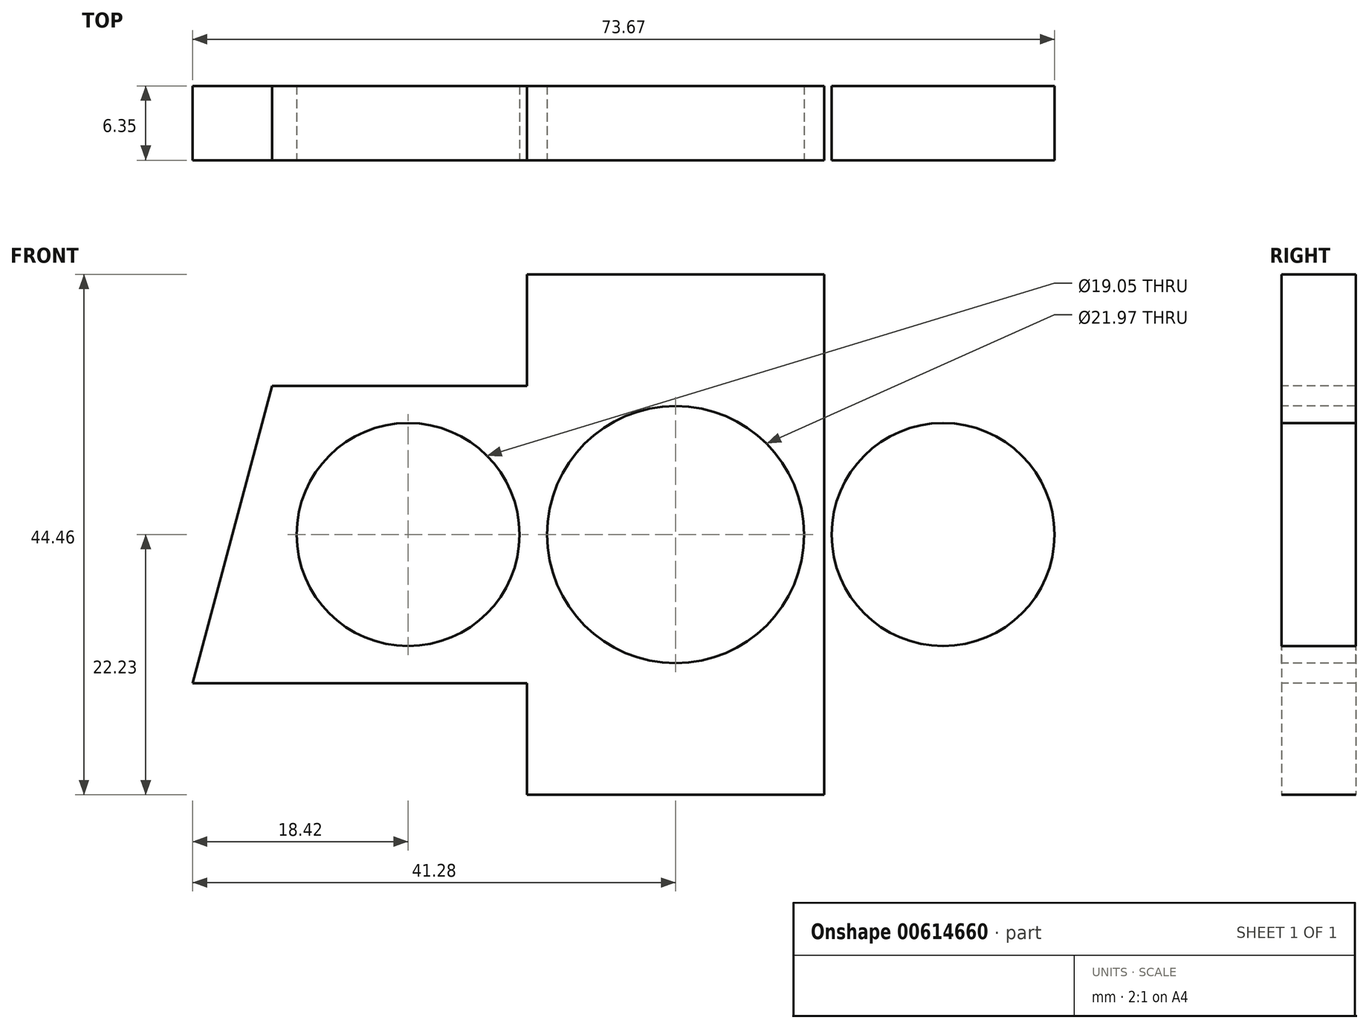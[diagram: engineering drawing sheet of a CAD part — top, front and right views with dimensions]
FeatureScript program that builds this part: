
annotation { "Feature Type Name" : "Feature", "Feature Type Description" : "" }
export const myFeature = defineFeature(function(context is Context, id is Id, definition is map)
    precondition{}
    {
        {
            var Q0;
            Q0=qCreatedBy(makeId("Front.planeOp"),FACE);
            var sketch = newSketch(context, id + "F0", { "sketchPlane" : qUnion([Q0])});
            skLineSegment(sketch, "E0.bottom", {"start": v(-50.8, 50.8) * mm, "end": v(50.8, 50.8) * mm});
            skLineSegment(sketch, "E0.top", {"start": v(-50.8, -50.8) * mm, "end": v(50.8, -50.8) * mm});
            skLineSegment(sketch, "E0.left", {"start": v(-50.8, 50.8) * mm, "end": v(-50.8, -50.8) * mm});
            skLineSegment(sketch, "E0.right", {"start": v(50.8, 50.8) * mm, "end": v(50.8, -50.8) * mm});
            skPoint(sketch, "E0.middle", {"position": v(0, 0) * mm});
            skSolve(sketch);
        }
        {
            var Q0;
            Q0=makeQuery(id+"F0.imprint","IMPRINT",FACE,{"disambiguationData":[TD([[makeQuery(id+"F0.imprint","IMPRINT",EDGE,{"derivedFrom":sQuery(id+"F0.wireOp",EDGE,"E0.bottom")}),-1.0]])]});
            extrude(context, id + "F1", {"entities" : qUnion([Q0]), "depth" : 6.35 * mm, "offsetDistance" : 25.4 * mm});
        }
        {
            var Q0;
            Q0=makeQuery(id+"F1.opExtrude","CAP_FACE",FACE,{"disambiguationData":[OSD([sQuery(id+"F0.wireOp",EDGE,"E0.bottom"),sQuery(id+"F0.wireOp",EDGE,"E0.top"),sQuery(id+"F0.wireOp",EDGE,"E0.left"),sQuery(id+"F0.wireOp",EDGE,"E0.right")])],"isStart":false});
            var sketch = newSketch(context, id + "F2", { "sketchPlane" : qUnion([Q0])});
            skCircle(sketch, "E1", {"center": v(0, 0) * mm, "radius": 10.99 * mm});
            skLineSegment(sketch, "E2", {"start": v(0, 19.05) * mm, "end": v(0, -38.1) * mm, "construction": true});
            skLineSegment(sketch, "E3", {"start": v(-41.28, 0) * mm, "end": v(41.28, 0) * mm, "construction": true});
            skLineSegment(sketch, "E4.bottom", {"start": v(-12.7, 22.23) * mm, "end": v(12.7, 22.23) * mm});
            skLineSegment(sketch, "E4.top", {"start": v(-12.7, -22.23) * mm, "end": v(12.7, -22.23) * mm});
            skLineSegment(sketch, "E4.left", {"start": v(-12.7, 22.23) * mm, "end": v(-12.7, -22.23) * mm});
            skLineSegment(sketch, "E4.right", {"start": v(12.7, 22.23) * mm, "end": v(12.7, -22.23) * mm});
            skLineSegment(sketch, "E5.bottom", {"start": v(-41.28, 12.7) * mm, "end": v(41.28, 12.7) * mm});
            skLineSegment(sketch, "E5.top", {"start": v(-41.28, -12.7) * mm, "end": v(41.28, -12.7) * mm});
            skLineSegment(sketch, "E5.left", {"start": v(-41.28, 12.7) * mm, "end": v(-41.28, -12.7) * mm});
            skLineSegment(sketch, "E5.right", {"start": v(41.28, 12.7) * mm, "end": v(41.28, -12.7) * mm});
            skLineSegment(sketch, "E6", {"start": v(-34.47, 12.7) * mm, "end": v(-41.28, -12.7) * mm});
            skLineSegment(sketch, "E7", {"start": v(41.28, 12.7) * mm, "end": v(34.47, -12.7) * mm});
            skCircle(sketch, "E8", {"center": v(-22.86, 0) * mm, "radius": 9.53 * mm});
            skCircle(sketch, "E9.MirrorC", {"center": v(22.86, 0) * mm, "radius": 9.53 * mm});
            skSolve(sketch);
        }
        {
            var Q0;
            {var subQ10=sQuery(id+"F2.wireOp",EDGE,"E4.bottom");Q0=makeQuery(id+"F2.imprint","IMPRINT",FACE,{"disambiguationData":[TD([[makeQuery(id+"F2.imprint","IMPRINT",EDGE,{"derivedFrom":subQ10}),1.0]])]});}
            var Q1;
            {var subQ0=sQuery(id+"F2.wireOp",EDGE,"E5.left");Q1=makeQuery(id+"F2.imprint","IMPRINT",FACE,{"disambiguationData":[TD([[makeQuery(id+"F2.imprint","IMPRINT",EDGE,{"derivedFrom":subQ0}),1.0]])]});}
            var Q2;
            Q2=makeQuery(id+"F2.imprint","IMPRINT",FACE,{"disambiguationData":[TD([[makeQuery(id+"F2.imprint","IMPRINT",EDGE,{"derivedFrom":sQuery(id+"F2.wireOp",EDGE,"E8")}),1.0]])]});
            var Q3;
            Q3=makeQuery(id+"F2.imprint","IMPRINT",FACE,{"disambiguationData":[TD([[makeQuery(id+"F2.imprint","IMPRINT",EDGE,{"derivedFrom":sQuery(id+"F2.wireOp",EDGE,"E1")}),1.0]])]});
            var Q4;
            Q4=makeQuery(id+"F2.imprint","IMPRINT",FACE,{"disambiguationData":[TD([[makeQuery(id+"F2.imprint","IMPRINT",EDGE,{"derivedFrom":sQuery(id+"F2.wireOp",EDGE,"E9.MirrorC")}),-1.0]])]});
            var Q5;
            {var subQ0=sQuery(id+"F2.wireOp",EDGE,"E5.right");Q5=makeQuery(id+"F2.imprint","IMPRINT",FACE,{"disambiguationData":[TD([[makeQuery(id+"F2.imprint","IMPRINT",EDGE,{"derivedFrom":subQ0}),-1.0]])]});}
            extrude(context, id + "F3", {"entities" : qUnion([Q0, Q1, Q2, Q3, Q4, Q5]), "operationType" : NewBodyOperationType.REMOVE, "oppositeDirection" : true, "depth" : 25.4 * mm, "offsetDistance" : 25.4 * mm});
        }
    });
